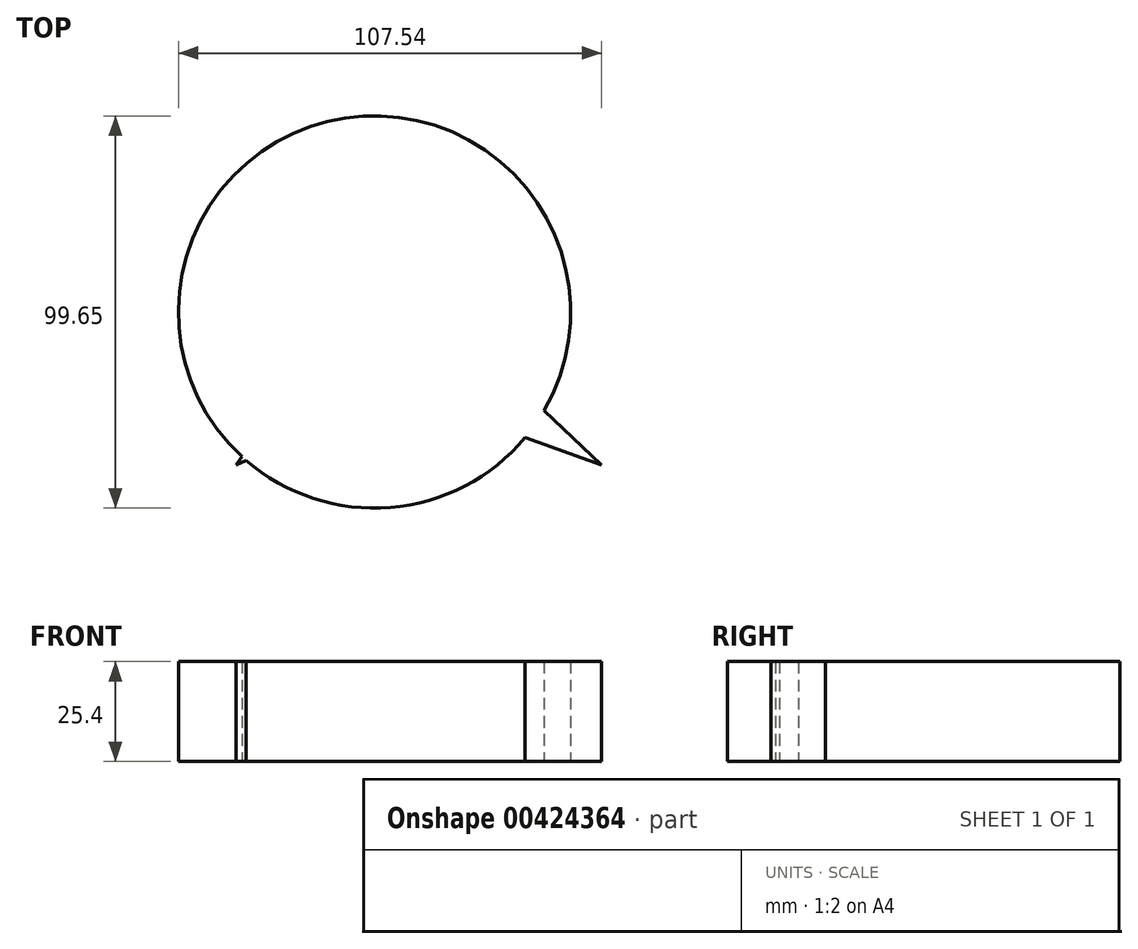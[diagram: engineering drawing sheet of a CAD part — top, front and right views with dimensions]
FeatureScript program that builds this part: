
annotation { "Feature Type Name" : "Feature", "Feature Type Description" : "" }
export const myFeature = defineFeature(function(context is Context, id is Id, definition is map)
    precondition{}
    {
        {
            var Q0;
            Q0=qCreatedBy(makeId("Top.planeOp"),FACE);
            var sketch = newSketch(context, id + "F0", { "sketchPlane" : qUnion([Q0])});
            skLineSegment(sketch, "E0", {"start": v(-9.73, 13.43) * mm, "end": v(0, 55.87) * mm});
            skLineSegment(sketch, "E1", {"start": v(-0.2, 56.07) * mm, "end": v(11.49, 13.43) * mm});
            skLineSegment(sketch, "E2", {"start": v(11.49, 13.43) * mm, "end": v(8.57, 11.1) * mm});
            skLineSegment(sketch, "E3", {"start": v(8.57, 11.1) * mm, "end": v(8.57, 7.2) * mm});
            skLineSegment(sketch, "E4", {"start": v(8.57, 7.2) * mm, "end": v(11.49, 4.48) * mm});
            skLineSegment(sketch, "E5", {"start": v(10.9, 4.48) * mm, "end": v(14.6, 4.87) * mm});
            skLineSegment(sketch, "E6", {"start": v(14.6, 4.87) * mm, "end": v(52.37, -30.76) * mm});
            skLineSegment(sketch, "E7", {"start": v(52.37, -30.76) * mm, "end": v(0, -12.07) * mm});
            skLineSegment(sketch, "E8", {"start": v(0.97, -12.07) * mm, "end": v(-40.5, -30.76) * mm});
            skLineSegment(sketch, "E9", {"start": v(-40.5, -30.76) * mm, "end": v(-16.16, 4.48) * mm});
            skLineSegment(sketch, "E10", {"start": v(-16.16, 4.48) * mm, "end": v(-9.73, 4.48) * mm});
            skLineSegment(sketch, "E11", {"start": v(-11.1, 4.87) * mm, "end": v(-13.63, 7.2) * mm});
            skLineSegment(sketch, "E12", {"start": v(-13.63, 7.2) * mm, "end": v(-9.22, 15.65) * mm});
            skCircle(sketch, "E13", {"center": v(-5.35, 8.06) * mm, "radius": 49.82 * mm});
            skSolve(sketch);
        }
        {
            var Q0;
            Q0 = qSketchRegion(id + "F0", true);
            extrude(context, id + "F1", {"entities" : qUnion([Q0]), "depth" : 25.4 * mm});
        }
    });
